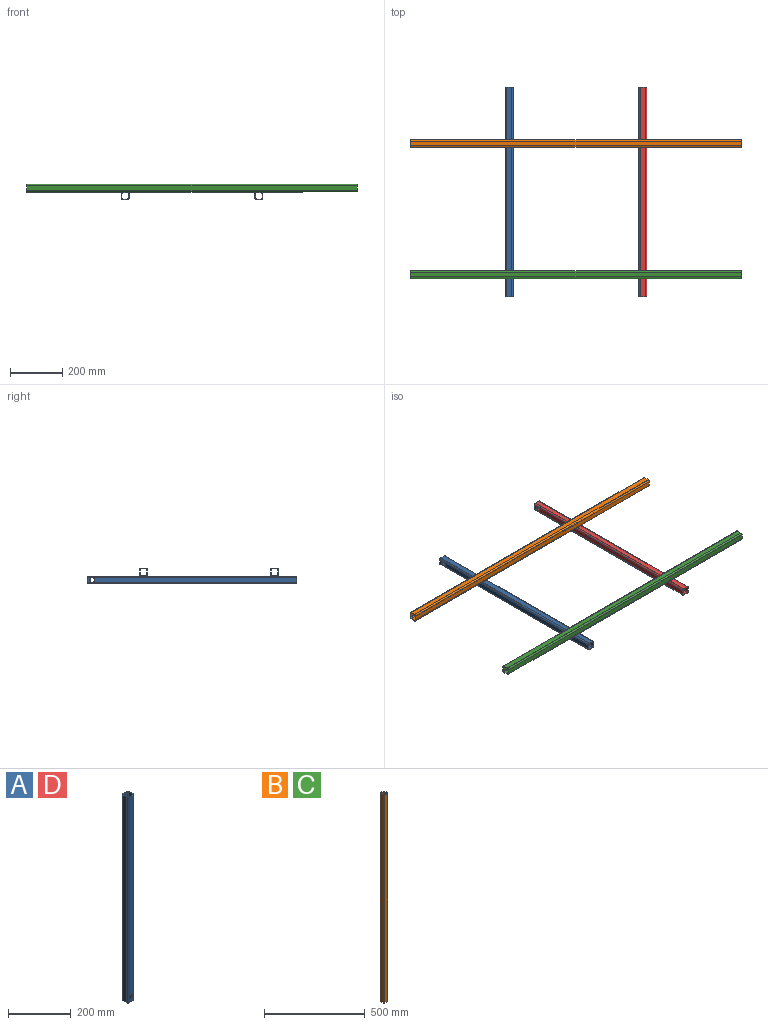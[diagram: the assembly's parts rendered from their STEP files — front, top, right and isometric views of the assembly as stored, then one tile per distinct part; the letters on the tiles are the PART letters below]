
ASSEMBLY  parts=4 mates=3
PART A: 24 faces, bbox 30x30x800 mm
  f0: plane 780x18mm, normal (0,1,0), area 13912.8mm2, adj f4,f10,f11,f23
  f1: plane 780x18mm, normal (0,-1,0), area 13912.8mm2, adj f4,f12,f13,f22
  f2: plane 780x18mm, normal (0,-1,0), area 13912.8mm2, adj f4,f18,f19,f23
  f3: plane 780x18mm, normal (0,1,0), area 13912.8mm2, adj f4,f20,f21,f22
  f4: plane 30x30mm, normal (0,0,1), area 300.8mm2, adj f0,f1,f2,f3,f6,f8,f10,f11
  f5: plane 30x30mm, normal (0,0,-1), area 300.8mm2, adj f6,f7,f8,f9,f10,f11,f12,f13
  f6: plane 800x18mm, normal (1,0,0), area 14400mm2, adj f4,f5,f10,f13
  f7: plane 20x18mm, normal (0,1,0), area 232.8mm2, adj f5,f10,f11,f23
  f8: plane 800x18mm, normal (-1,0,0), area 14400mm2, adj f4,f5,f11,f12
  f9: plane 20x18mm, normal (0,-1,0), area 232.8mm2, adj f5,f12,f13,f22
  f10: cylinder r=6mm len=800mm, axis (0,0,1), area 7539.8mm2, adj f0,f4,f5,f6,f7
  f11: cylinder r=6mm len=800mm, axis (0,0,-1), area 7539.8mm2, adj f0,f4,f5,f7,f8
  f12: cylinder r=6mm len=800mm, axis (0,0,1), area 7539.8mm2, adj f1,f4,f5,f8,f9
  f13: cylinder r=6mm len=800mm, axis (0,0,-1), area 7539.8mm2, adj f1,f4,f5,f6,f9
  f14: plane 800x18mm, normal (-1,0,0), area 14400mm2, adj f4,f5,f18,f21
  f15: plane 20x18mm, normal (0,-1,0), area 232.8mm2, adj f5,f18,f19,f23
  f16: plane 800x18mm, normal (1,0,0), area 14400mm2, adj f4,f5,f19,f20
  f17: plane 20x18mm, normal (0,1,0), area 232.8mm2, adj f5,f20,f21,f22
  f18: cylinder r=3mm len=800mm, axis (0,0,1), area 3769.9mm2, adj f2,f4,f5,f14,f15
  f19: cylinder r=3mm len=800mm, axis (0,0,-1), area 3769.9mm2, adj f2,f4,f5,f15,f16
  f20: cylinder r=3mm len=800mm, axis (0,0,1), area 3769.9mm2, adj f3,f4,f5,f16,f17
  f21: cylinder r=3mm len=800mm, axis (0,0,-1), area 3769.9mm2, adj f3,f4,f5,f14,f17
  f22: cylinder r=9mm len=18mm, axis (0,-1,0), area 169.6mm2, adj f1,f3,f9,f17
  f23: cylinder r=9mm len=18mm, axis (0,-1,0), area 169.6mm2, adj f0,f2,f7,f15
PART B: 18 faces, bbox 30x30x1260 mm
  f0: plane 30x30mm, normal (0,0,1), area 300.8mm2, adj f2,f3,f4,f5,f6,f7,f8,f9
  f1: plane 30x30mm, normal (0,0,-1), area 300.8mm2, adj f2,f3,f4,f5,f6,f7,f8,f9
  f2: plane 1260x18mm, normal (1,0,0), area 22680mm2, adj f0,f1,f6,f9
  f3: plane 1260x18mm, normal (0,1,0), area 22680mm2, adj f0,f1,f6,f7
  f4: plane 1260x18mm, normal (-1,0,0), area 22680mm2, adj f0,f1,f7,f8
  f5: plane 1260x18mm, normal (0,-1,0), area 22680mm2, adj f0,f1,f8,f9
  f6: cylinder r=6mm len=1260mm, axis (0,0,1), area 11875.2mm2, adj f0,f1,f2,f3
  f7: cylinder r=6mm len=1260mm, axis (0,0,-1), area 11875.2mm2, adj f0,f1,f3,f4
  f8: cylinder r=6mm len=1260mm, axis (0,0,1), area 11875.2mm2, adj f0,f1,f4,f5
  f9: cylinder r=6mm len=1260mm, axis (0,0,-1), area 11875.2mm2, adj f0,f1,f2,f5
  f10: plane 1260x18mm, normal (-1,0,0), area 22680mm2, adj f0,f1,f14,f17
  f11: plane 1260x18mm, normal (0,-1,0), area 22680mm2, adj f0,f1,f14,f15
  f12: plane 1260x18mm, normal (1,0,0), area 22680mm2, adj f0,f1,f15,f16
  f13: plane 1260x18mm, normal (0,1,0), area 22680mm2, adj f0,f1,f16,f17
  f14: cylinder r=3mm len=1260mm, axis (0,0,1), area 5937.6mm2, adj f0,f1,f10,f11
  f15: cylinder r=3mm len=1260mm, axis (0,0,-1), area 5937.6mm2, adj f0,f1,f11,f12
  f16: cylinder r=3mm len=1260mm, axis (0,0,1), area 5937.6mm2, adj f0,f1,f12,f13
  f17: cylinder r=3mm len=1260mm, axis (0,0,-1), area 5937.6mm2, adj f0,f1,f10,f13
PART C: same geometry as B
PART D: same geometry as A
PLACE A rot(axis=(0.58,0.58,-0.58),120deg) t=(360,-183.53,612)mm
PLACE B rot(axis=(0,1,0),90deg) t=(-15,-398.53,642)mm fixed
PLACE C rot(axis=(0,1,0),90deg) t=(-15,-898.53,642)mm
PLACE D rot(axis=(0.58,0.58,-0.58),120deg) t=(870,-183.53,612)mm
MATE parallel A.f5 <-> B.f3  axis (0,1,0) through (360,-183.53,600)mm
MATE planar A.f8 <-> B.f2  axis (0,0,1) through (360,-583.53,627)mm
MATE parallel B.f1 <-> A.f1  axis (-1,0,0) through (-15,-398.53,642)mm
